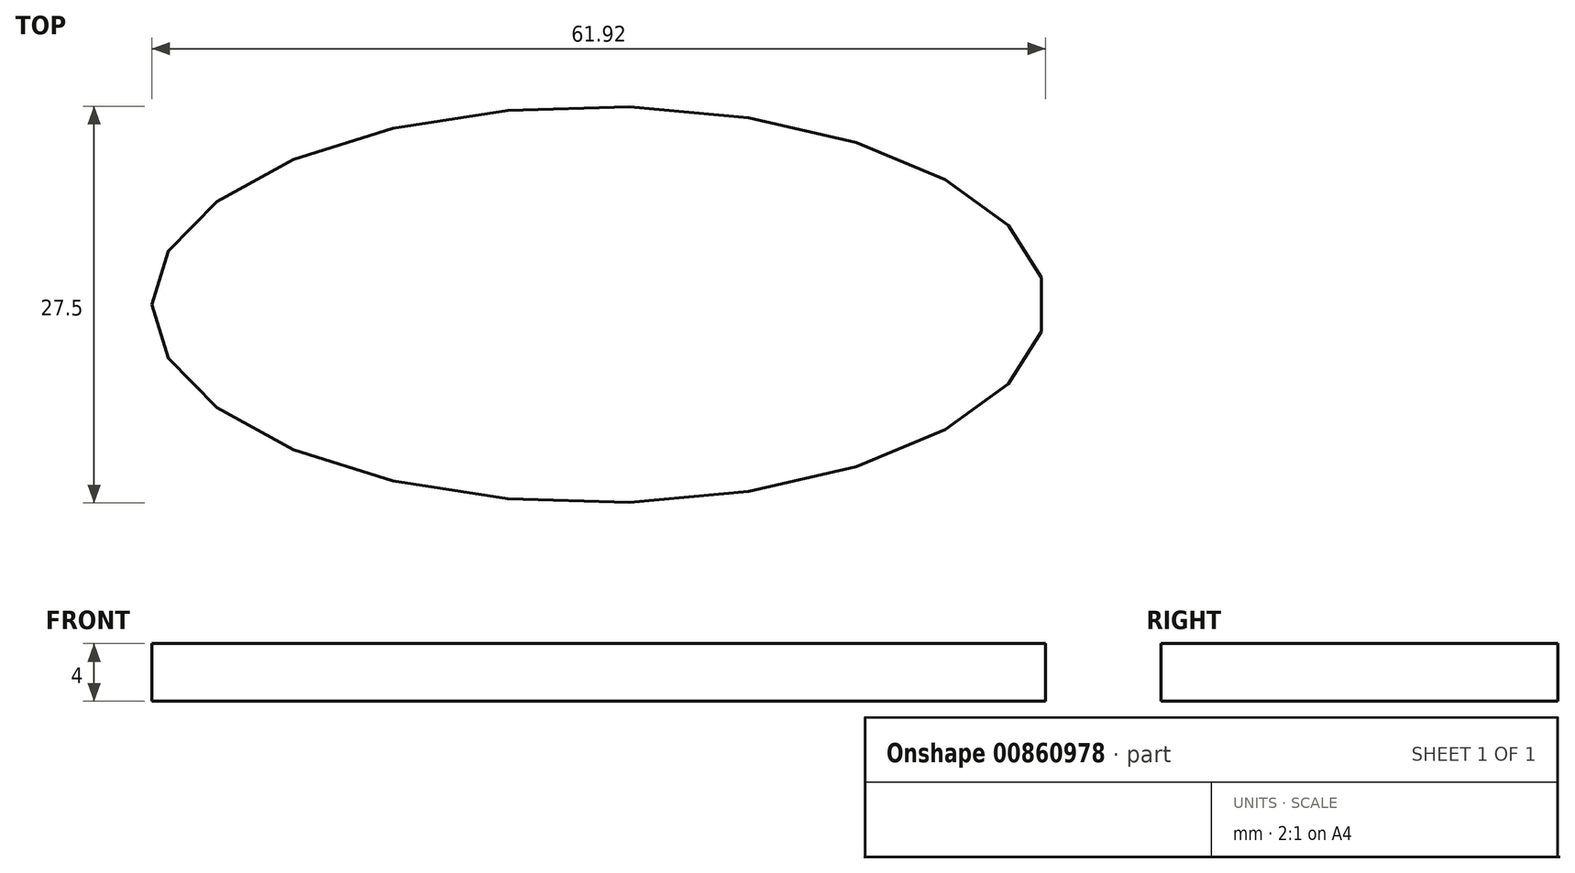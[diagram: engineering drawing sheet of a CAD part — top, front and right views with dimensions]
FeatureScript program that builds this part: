
annotation { "Feature Type Name" : "Feature", "Feature Type Description" : "" }
export const myFeature = defineFeature(function(context is Context, id is Id, definition is map)
    precondition{}
    {
        {
            var Q0;
            Q0=qCreatedBy(makeId("Top.planeOp"),FACE);
            var sketch = newSketch(context, id + "F0", { "sketchPlane" : qUnion([Q0])});
            skEllipse(sketch, "E0", {"center": v(0, 0) * mm, "majorRadius": 30.96 * mm, "minorRadius": 13.75 * mm, "majorAxis": v(-1, 0)});
            skSolve(sketch);
        }
        {
            var Q0;
            Q0 = qSketchRegion(id + "F0", true);
            extrude(context, id + "F1", {"entities" : qUnion([Q0]), "depth" : 4 * mm, "offsetDistance" : 25 * mm});
        }
    });
